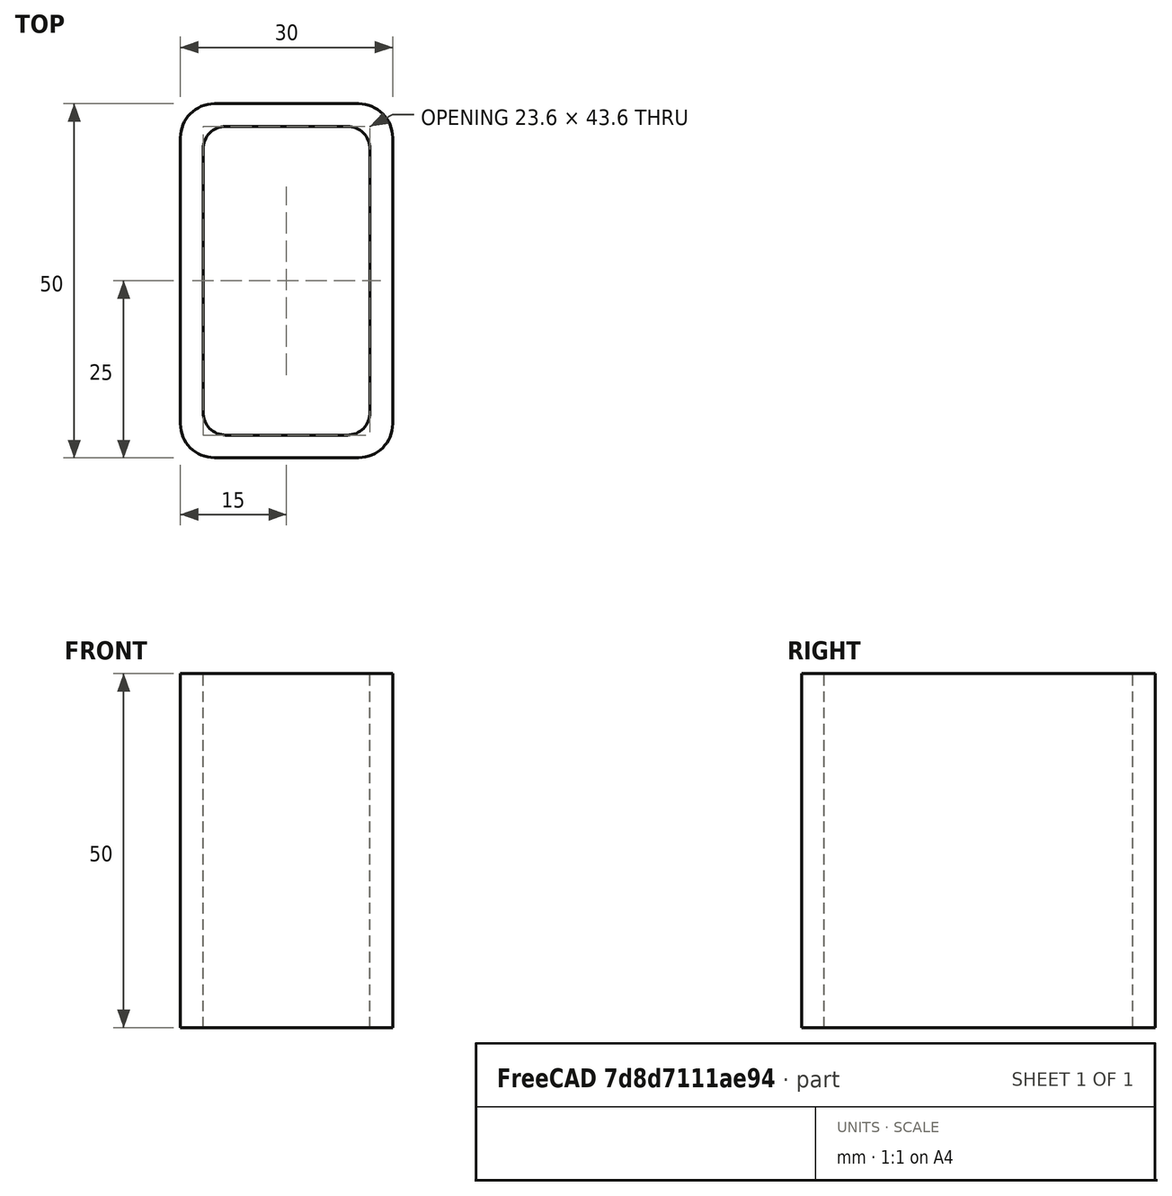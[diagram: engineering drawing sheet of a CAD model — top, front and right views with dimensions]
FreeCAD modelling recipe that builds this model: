
FCSTD DOCUMENT  (FreeCAD 0.15R4671 (Git))
Label: Rectangular hollow section 50x30x3.2 EN10219 S235JRH
License: All rights reserved
LicenseURL: http://en.wikipedia.org/wiki/All_rights_reserved
objects: Sketcher::SketchObject×1, Part::Extrusion×1
note: 2 computed .brp shape members not serialized (recipe doc carries the construction recipe); baked Part::Feature solids carry a one-line shape summary decoded from their .brp

FEATURE [Sketcher::SketchObject] Sketch
  sketch-geometry (16):
    g0: LineSegment StartX=-8.6 StartY=21.8 StartZ=0 EndX=8.6 EndY=21.8 EndZ=0
    g1: LineSegment StartX=11.8 StartY=18.6 StartZ=0 EndX=11.8 EndY=-18.6 EndZ=0
    g2: LineSegment StartX=8.6 StartY=-21.8 StartZ=0 EndX=-8.6 EndY=-21.8 EndZ=0
    g3: LineSegment StartX=-11.8 StartY=-18.6 StartZ=0 EndX=-11.8 EndY=18.6 EndZ=0
    g4: LineSegment StartX=-10.2 StartY=25 StartZ=0 EndX=10.2 EndY=25 EndZ=0
    g5: LineSegment StartX=15 StartY=20.2 StartZ=0 EndX=15 EndY=-20.2 EndZ=0
    g6: LineSegment StartX=10.2 StartY=-25 StartZ=0 EndX=-10.2 EndY=-25 EndZ=0
    g7: LineSegment StartX=-15 StartY=-20.2 StartZ=0 EndX=-15 EndY=20.2 EndZ=0
    g8: ArcOfCircle CenterX=-8.6 CenterY=18.6 CenterZ=0 NormalX=0 NormalY=0 NormalZ=1 Radius=3.2 StartAngle=1.5708 EndAngle=3.14159
    g9: ArcOfCircle CenterX=8.6 CenterY=18.6 CenterZ=0 NormalX=0 NormalY=0 NormalZ=1 Radius=3.2 StartAngle=0 EndAngle=1.5708
    g10: ArcOfCircle CenterX=8.6 CenterY=-18.6 CenterZ=0 NormalX=0 NormalY=0 NormalZ=1 Radius=3.2 StartAngle=4.71239 EndAngle=6.28319
    g11: ArcOfCircle CenterX=-8.6 CenterY=-18.6 CenterZ=0 NormalX=0 NormalY=0 NormalZ=1 Radius=3.2 StartAngle=3.14159 EndAngle=4.71239
    g12: ArcOfCircle CenterX=10.2 CenterY=20.2 CenterZ=0 NormalX=0 NormalY=0 NormalZ=1 Radius=4.8 StartAngle=0 EndAngle=1.5708
    g13: ArcOfCircle CenterX=10.2 CenterY=-20.2 CenterZ=0 NormalX=0 NormalY=0 NormalZ=1 Radius=4.8 StartAngle=4.71239 EndAngle=6.28319
    g14: ArcOfCircle CenterX=-10.2 CenterY=-20.2 CenterZ=0 NormalX=0 NormalY=0 NormalZ=1 Radius=4.8 StartAngle=3.14159 EndAngle=4.71239
    g15: ArcOfCircle CenterX=-10.2 CenterY=20.2 CenterZ=0 NormalX=0 NormalY=0 NormalZ=1 Radius=4.8 StartAngle=1.5708 EndAngle=3.14159
  constraints (36):
    c: Horizontal(g2)
    c: Vertical(g3)
    c: Horizontal(g6)
    c: Vertical(g7)
    c: Tangent(g3,g8) = 1.5708
    c: Tangent(g0,g8) = 1.5708
    c: Tangent(g0,g9) = 1.5708
    c: Tangent(g1,g9) = 1.5708
    c: Tangent(g1,g10) = 1.5708
    c: Tangent(g2,g10) = 1.5708
    c: Tangent(g2,g11) = 1.5708
    c: Tangent(g3,g11) = 1.5708
    c: Tangent(g4,g12) = 1.5708
    c: Tangent(g5,g12) = 1.5708
    c: Tangent(g5,g13) = 1.5708
    c: Tangent(g6,g13) = 1.5708
    c: Tangent(g6,g14) = 1.5708
    c: Tangent(g7,g14) = 1.5708
    c: Tangent(g7,g15) = 1.5708
    c: Tangent(g4,g15) = 1.5708
    c: Equal(g9,g8)
    c: Equal(g9,g11)
    c: Equal(g9,g10)
    c: Equal(g12,g15)
    c: Equal(g12,g14)
    c: Equal(g12,g13)
    c: Symmetric(g4,g6,g-1)
    c: Symmetric(g7,g5,g-2)
    c: DistanceY(g4,g6) = -50
    c: DistanceX(g7,g5) = 30
    c: Symmetric(g3,g1,g-2)
    c: Symmetric(g0,g2,g-1)
    c: DistanceY(g0,g4) = 3.2
    c: DistanceX(g5,g1) = -3.2
    c: Radius(g9) = 3.2
    c: Radius(g12) = 4.8
FEATURE [Part::Extrusion] Extrude  label="Rectangular hollow section 50x30x3.2 EN10219 S235JRH"
  Base = -> Sketch
  Dir = (0,0,50)
  Solid = true
